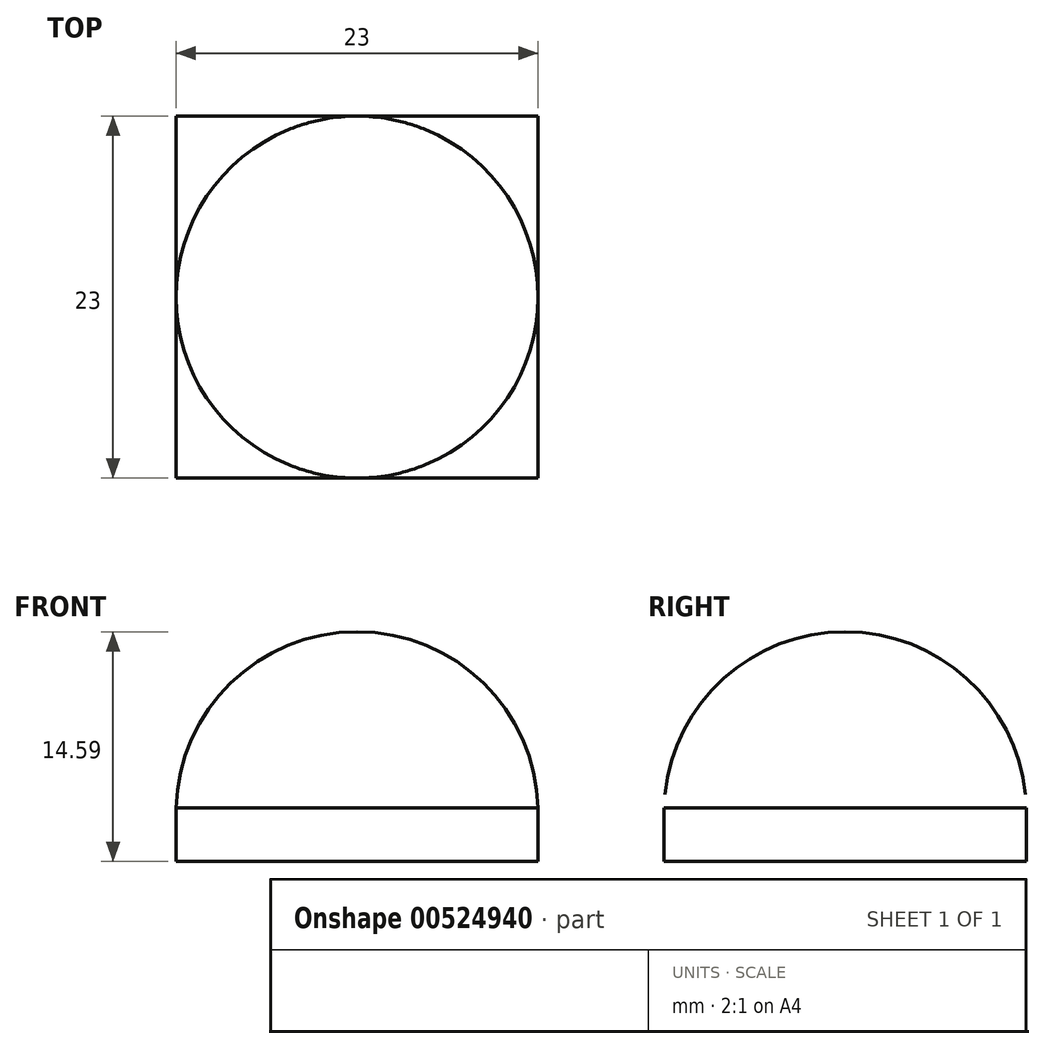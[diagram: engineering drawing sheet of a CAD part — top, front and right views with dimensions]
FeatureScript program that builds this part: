
annotation { "Feature Type Name" : "Feature", "Feature Type Description" : "" }
export const myFeature = defineFeature(function(context is Context, id is Id, definition is map)
    precondition{}
    {
        {
            var Q0;
            Q0=qCreatedBy(makeId("Top.planeOp"),FACE);
            var sketch = newSketch(context, id + "F0", { "sketchPlane" : qUnion([Q0])});
            skLineSegment(sketch, "E0.bottom", {"start": v(11.5, -11.5) * mm, "end": v(-11.5, -11.5) * mm});
            skLineSegment(sketch, "E0.top", {"start": v(11.5, 11.5) * mm, "end": v(-11.5, 11.5) * mm});
            skLineSegment(sketch, "E0.left", {"start": v(11.5, -11.5) * mm, "end": v(11.5, 11.5) * mm});
            skLineSegment(sketch, "E0.right", {"start": v(-11.5, -11.5) * mm, "end": v(-11.5, 11.5) * mm});
            skPoint(sketch, "E0.middle", {"position": v(0, 0) * mm});
            skSolve(sketch);
        }
        {
            var Q0;
            Q0=makeQuery(id+"F0.imprint","IMPRINT",FACE,{"disambiguationData":[TD([[makeQuery(id+"F0.imprint","IMPRINT",EDGE,{"derivedFrom":sQuery(id+"F0.wireOp",EDGE,"E0.bottom")}),-1.0]])]});
            extrude(context, id + "F1", {"entities" : qUnion([Q0]), "depth" : 3.4 * mm, "offsetDistance" : 25 * mm});
        }
        {
            var Q0;
            Q0=makeQuery(id+"F1.opExtrude","CAP_FACE",FACE,{"disambiguationData":[OSD([sQuery(id+"F0.wireOp",EDGE,"E0.bottom"),sQuery(id+"F0.wireOp",EDGE,"E0.top"),sQuery(id+"F0.wireOp",EDGE,"E0.left"),sQuery(id+"F0.wireOp",EDGE,"E0.right")])],"isStart":false});
            cPlane(context, id + "F2", {"entities" : qUnion([Q0]), "cplaneType" : CPlaneType.OFFSET, "offset" : 0.3 * mm, "oppositeDirection" : true, "width" : 150 * mm, "height" : 150 * mm});
        }
        {
            var Q0;
            Q0=qCreatedBy(id+"F2.planeOp",FACE);
            var sketch = newSketch(context, id + "F3", { "sketchPlane" : qUnion([Q0])});
            skArc(sketch, "E1", {"start": v(0, -11.5) * mm, "mid": v(11.5, 0) * mm, "end": v(0, 11.5) * mm});
            skLineSegment(sketch, "E2", {"start": v(0, 11.5) * mm, "end": v(0, -11.5) * mm});
            skSolve(sketch);
        }
        {
            var Q0;
            Q0=makeQuery(id+"F3.imprint","IMPRINT",FACE,{"disambiguationData":[TD([[makeQuery(id+"F3.imprint","IMPRINT",EDGE,{"derivedFrom":sQuery(id+"F3.wireOp",EDGE,"E1")}),1.0]])]});
            var Q1;
            Q1=sQuery(id+"F3.wireOp",EDGE,"E2");
            revolve(context, id + "F4", {"operationType" : NewBodyOperationType.ADD, "entities" : qUnion([Q0]), "axis" : qUnion([Q1]), "revolveType" : RevolveType.FULL});
        }
        {
            var Q0;
            Q0=makeQuery(id+"F1.opExtrude","CAP_FACE",FACE,{"disambiguationData":[OSD([sQuery(id+"F0.wireOp",EDGE,"E0.bottom"),sQuery(id+"F0.wireOp",EDGE,"E0.top"),sQuery(id+"F0.wireOp",EDGE,"E0.left"),sQuery(id+"F0.wireOp",EDGE,"E0.right")])],"isStart":true});
            cPlane(context, id + "F5", {"entities" : qUnion([Q0]), "cplaneType" : CPlaneType.OFFSET, "offset" : 0 * mm, "width" : 150 * mm, "height" : 150 * mm});
        }
        {
            var Q0;
            Q0=qCreatedBy(id+"F5.planeOp",FACE);
            var sketch = newSketch(context, id + "F6", { "sketchPlane" : qUnion([Q0])});
            skLineSegment(sketch, "E3.bottom", {"start": v(11.5, -11.5) * mm, "end": v(-11.5, -11.5) * mm});
            skLineSegment(sketch, "E3.top", {"start": v(11.5, 11.5) * mm, "end": v(-11.5, 11.5) * mm});
            skLineSegment(sketch, "E3.left", {"start": v(11.5, -11.5) * mm, "end": v(11.5, 11.5) * mm});
            skLineSegment(sketch, "E3.right", {"start": v(-11.5, -11.5) * mm, "end": v(-11.5, 11.5) * mm});
            skPoint(sketch, "E3.middle", {"position": v(0, 0) * mm});
            skSolve(sketch);
        }
        {
            var Q0;
            Q0=makeQuery(id+"F6.imprint","IMPRINT",FACE,{"disambiguationData":[TD([[makeQuery(id+"F6.imprint","IMPRINT",EDGE,{"derivedFrom":sQuery(id+"F6.wireOp",EDGE,"E3.bottom")}),-1.0]])]});
            extrude(context, id + "F7", {"entities" : qUnion([Q0]), "operationType" : NewBodyOperationType.REMOVE, "depth" : 25 * mm, "offsetDistance" : 25 * mm});
        }
    });
